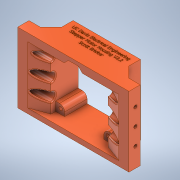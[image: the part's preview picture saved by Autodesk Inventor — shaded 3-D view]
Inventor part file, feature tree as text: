
AUTODESK INVENTOR PART (.ipt)
format: ipt  version: 2020 (Build 240168000, 168)  size: 3,643,392 bytes
history: native  units: mm
features: sketch x9, extrude x7, projected_geometry x7, emboss x2, chamfer x1, fillet x1
ambient origin geometry x8: Origin, YZ Plane, XZ Plane, XY Plane, X Axis, Y Axis, Z Axis, Center Point
bodies: Solid1 (feature_tree)
feature tree (27):
  extrude  "Extrusion1"  Depth=70.0mm
  extrude  "Extrusion2"  Depth=33.4mm TaperAngle=0.0deg
  extrude  "Extrusion3"  Depth=33.65mm
  extrude  "Extrusion4"  Depth=11.6mm
  extrude  "Extrusion5"  Depth=10.5mm
  extrude  "Extrusion8"  Depth=10.5mm
  extrude  "Extrusion9"  Depth=70.0mm TaperAngle=0.0deg
  chamfer  "Chamfer2"  Distance=28.65mm
  fillet  "Fillet1"  Radius=57.3mm
  emboss  "Emboss1"
  emboss  "Emboss2"
  sketch  "Sketch1"  dims[d0=55.65mm d1=70.0mm]
  sketch  "Sketch2"  dims[d2=111.3mm d3=33.4mm d4=0.0mm]
  projected_geometry  "Projected Loop1"
  sketch  "Sketch3"  dims[d5=55.65mm d6=33.65mm]
  projected_geometry  "Projected Loop2"
  sketch  "Sketch4"  dims[d10=33.65mm d13=11.6mm]
  sketch  "Sketch6"  dims[d14=10.5mm d15=10.5mm]
  projected_geometry  "Projected Loop5"
  sketch  "Sketch10"  dims[d16=11.6mm d17=10.5mm]
  sketch  "Sketch11"  dims[d18=10.5mm d19=70.0mm d20=0.0mm]
  projected_geometry  "Projected Loop8"
  projected_geometry  "Projected Loop9"
  sketch  "Sketch12"  dims[d21=55.65mm]
  projected_geometry  "Projected Loop12"
  sketch  "Sketch13"  dims[d22=5.0mm d23=28.65mm d24=57.3mm d25=57.3mm d26=68.0mm d27=0.0mm d28=6.4mm d29=33.65mm d30=17.0mm d31=34.0mm d32=3.25mm d33=3.25mm d34=3.25mm d35=115.0mm d36=0.0mm d37=7.5mm d38=9.0mm d39=9.0mm d40=101.3mm d41=0.0mm d57=1.0mm d60=1.0mm d61=0.0mm d62=60.0mm d63=3.65mm d65=3.635mm d66=3.65mm d67=3.65mm d68=60.0mm d69=90.0deg d70=1.0mm d71=0.0mm d72=23.65mm d73=4.2mm d74=10.0mm d81=9.0mm d82=9.0mm d83=9.0mm d84=9.0mm d85=9.0mm d86=9.0mm d87=9.0mm d88=9.0mm d89=5.08mm d90=5.08mm d91=3.5mm d92=5.08mm d93=5.08mm d94=3.5mm d95=3.5mm d96=3.5mm d97=5.0mm d98=22.5mm d99=0.0mm d100=6.0mm d101=6.0mm d102=6.0mm d103=6.0mm d104=5.0mm d105=0.0mm d106=17.0mm d107=2.0mm d108=3.490659mm d109=45.0deg d110=45.0deg d111=4.9mm d112=0.0mm d113=57.3mm d114=5.08mm d115=5.08mm d116=5.08mm d117=5.08mm]
  projected_geometry  "Projected Loop13"
